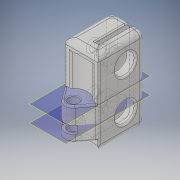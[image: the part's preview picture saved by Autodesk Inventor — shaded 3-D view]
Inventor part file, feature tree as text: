
AUTODESK INVENTOR PART (.ipt)
format: ipt  version: 2019 (Build 230136000, 136)  size: 371,200 bytes
history: native  units: mm
features: extrude x7, sketch x7, fillet x5, plane x2, other x1
ambient origin geometry x8: Origin, YZ Plane, XZ Plane, XY Plane, X Axis, Y Axis, Z Axis, Center Point
bodies: Body1 (feature_tree)
feature tree (22):
  other  "Sólido1"
  extrude  "Extrusión1"  Depth=3.8mm
  extrude  "Extrusión2"  Depth=1.5mm
  extrude  "Extrusión3"  Depth=30.0mm TaperAngle=0.0deg
  extrude  "Extrusión4"  Depth=7.0mm
  plane  "Plano de trabajo1"
  extrude  "Extrusión5"  Depth=10.0mm
  plane  "Plano de trabajo2"
  extrude  "Extrusión6"  Depth=7.2mm
  fillet  "Empalme1"  Radius=5.55mm
  fillet  "Empalme2"  Radius=10.0mm
  fillet  "Empalme5"  Radius=3.0mm
  fillet  "Empalme3"  Radius=6.0mm
  extrude  "Extrusión7"  Depth=1.0mm
  fillet  "Empalme4"  Radius=3.5mm
  sketch  "Boceto1"  dims[d1=17.0mm d2=3.8mm]
  sketch  "Boceto2"  dims[d3=6.7mm d4=1.5mm]
  sketch  "Boceto3"  dims[d6=3.8mm d7=30.0mm d8=0.0mm]
  sketch  "Boceto4"  dims[d9=3.5mm d10=7.0mm]
  sketch  "Boceto5"  dims[d11=7.5mm d12=20.0mm d14=15.0mm d15=10.0mm d17=10.0mm]
  sketch  "Boceto6"  dims[d19=30.0mm d20=0.0mm d21=7.2mm]
  sketch  "Boceto7"  dims[d22=7.2mm d23=30.0mm d24=0.0mm d26=5.55mm d27=20.0mm d29=15.0mm d30=10.0mm d32=10.0mm d34=3.0mm d35=0.0mm d36=6.0mm d37=3.0mm d38=3.5mm d39=11.5mm d40=0.0mm d42=2.8mm d43=0.0mm d44=6.0mm d46=2.75mm d47=2.75mm d48=30.0deg d49=30.0deg d51=7.0mm d52=2.0mm d53=0.6mm d54=0.4mm d55=60.0deg d56=11.0mm d57=0.0mm d58=1.0mm d59=0.3mm]
